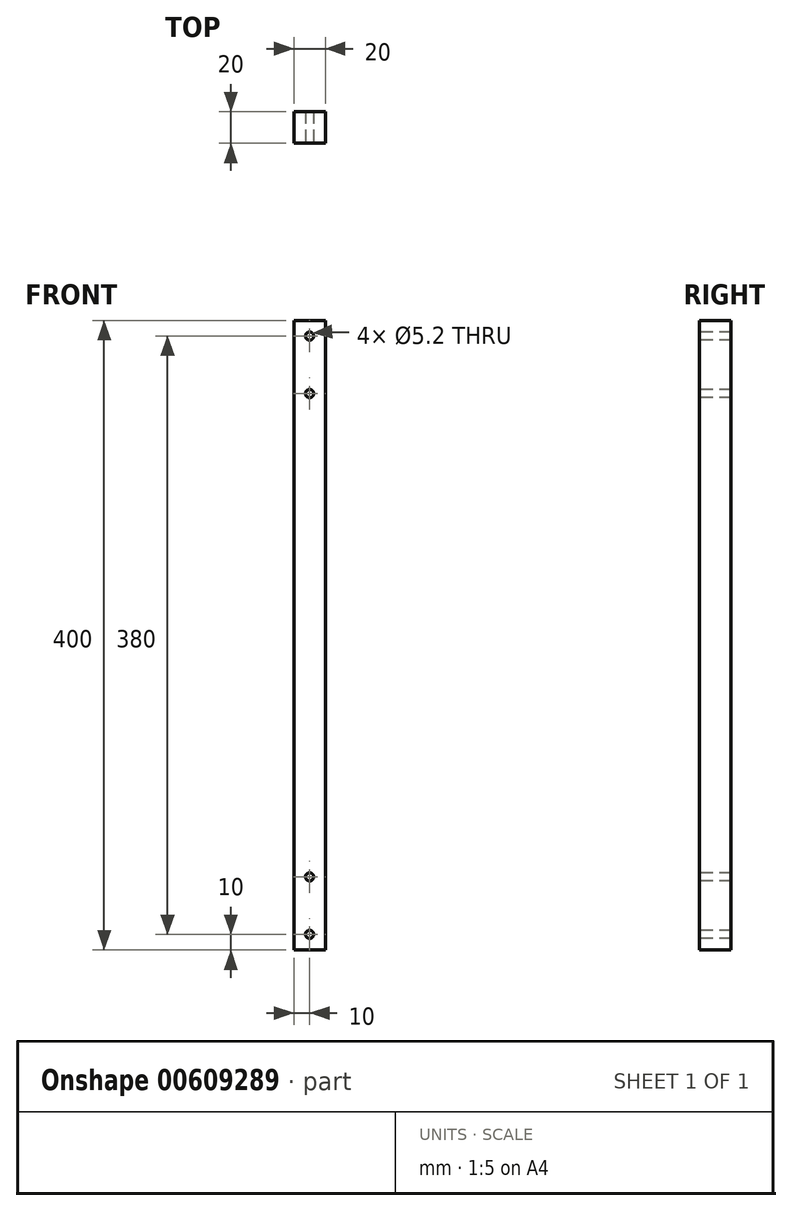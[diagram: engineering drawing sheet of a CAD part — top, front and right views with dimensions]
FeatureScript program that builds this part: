
annotation { "Feature Type Name" : "Feature", "Feature Type Description" : "" }
export const myFeature = defineFeature(function(context is Context, id is Id, definition is map)
    precondition{}
    {
        {
            var Q0;
            Q0=qCreatedBy(makeId("Top.planeOp"),FACE);
            var sketch = newSketch(context, id + "F0", { "sketchPlane" : qUnion([Q0])});
            skLineSegment(sketch, "E0.bottom", {"start": v(0, 0) * mm, "end": v(20, 0) * mm});
            skLineSegment(sketch, "E0.top", {"start": v(0, -20) * mm, "end": v(20, -20) * mm});
            skLineSegment(sketch, "E0.left", {"start": v(0, 0) * mm, "end": v(0, -20) * mm});
            skLineSegment(sketch, "E0.right", {"start": v(20, 0) * mm, "end": v(20, -20) * mm});
            skSolve(sketch);
        }
        {
            var Q0;
            Q0=makeQuery(id+"F0.imprint","IMPRINT",FACE,{"disambiguationData":[TD([[makeQuery(id+"F0.imprint","IMPRINT",EDGE,{"derivedFrom":sQuery(id+"F0.wireOp",EDGE,"E0.bottom")}),-1.0]])]});
            extrude(context, id + "F1", {"entities" : qUnion([Q0]), "depth" : 400 * mm, "offsetDistance" : 25 * mm});
        }
        {
            var Q0;
            Q0=makeQuery(id+"F1.opExtrude","SWEPT_FACE",FACE,{"disambiguationData":[OSD([sQuery(id+"F0.wireOp",EDGE,"E0.top")])]});
            var sketch = newSketch(context, id + "F2", { "sketchPlane" : qUnion([Q0])});
            skCircle(sketch, "E1", {"center": v(10, 10) * mm, "radius": 2.6 * mm});
            skCircle(sketch, "E2", {"center": v(10, 390) * mm, "radius": 2.6 * mm});
            skCircle(sketch, "E3", {"center": v(10, 353.5) * mm, "radius": 2.6 * mm});
            skCircle(sketch, "E4", {"center": v(10, 46.5) * mm, "radius": 2.6 * mm});
            skSolve(sketch);
        }
        {
            var Q0;
            Q0=makeQuery(id+"F2.imprint","IMPRINT",FACE,{"disambiguationData":[TD([[makeQuery(id+"F2.imprint","IMPRINT",EDGE,{"derivedFrom":sQuery(id+"F2.wireOp",EDGE,"E1")}),1.0]])]});
            var Q1;
            Q1=makeQuery(id+"F2.imprint","IMPRINT",FACE,{"disambiguationData":[TD([[makeQuery(id+"F2.imprint","IMPRINT",EDGE,{"derivedFrom":sQuery(id+"F2.wireOp",EDGE,"E2")}),1.0]])]});
            var Q2;
            Q2=makeQuery(id+"F2.imprint","IMPRINT",FACE,{"disambiguationData":[TD([[makeQuery(id+"F2.imprint","IMPRINT",EDGE,{"derivedFrom":sQuery(id+"F2.wireOp",EDGE,"E3")}),1.0]])]});
            var Q3;
            Q3=makeQuery(id+"F2.imprint","IMPRINT",FACE,{"disambiguationData":[TD([[makeQuery(id+"F2.imprint","IMPRINT",EDGE,{"derivedFrom":sQuery(id+"F2.wireOp",EDGE,"E4")}),1.0]])]});
            extrude(context, id + "F3", {"entities" : qUnion([Q0, Q1, Q2, Q3]), "operationType" : NewBodyOperationType.REMOVE, "oppositeDirection" : true, "depth" : 20 * mm, "offsetDistance" : 25 * mm});
        }
    });
